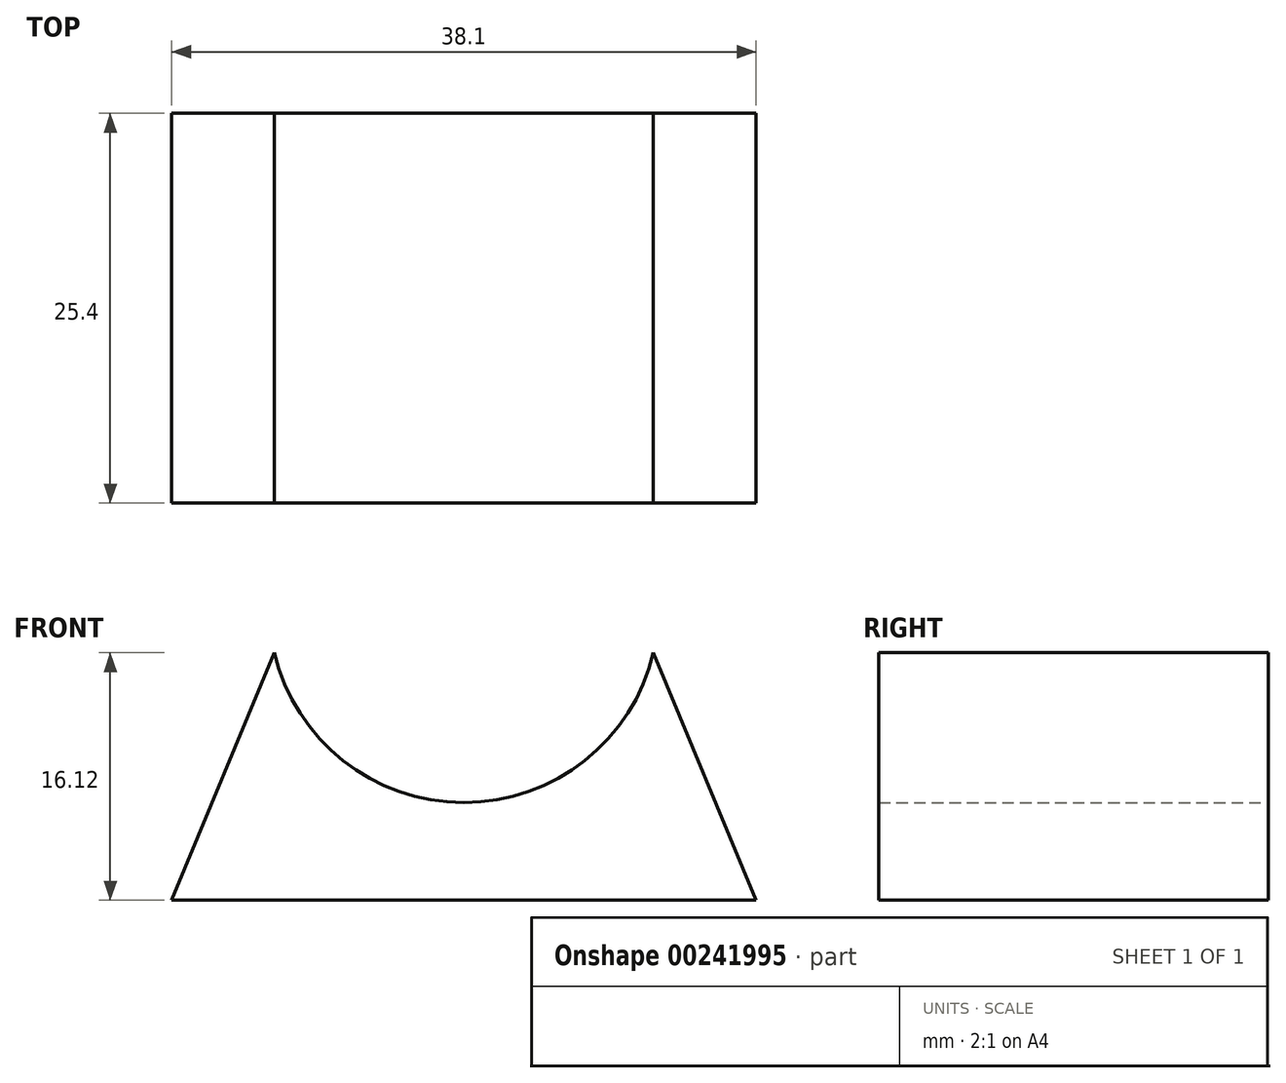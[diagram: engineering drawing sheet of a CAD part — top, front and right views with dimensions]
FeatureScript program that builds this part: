
annotation { "Feature Type Name" : "Feature", "Feature Type Description" : "" }
export const myFeature = defineFeature(function(context is Context, id is Id, definition is map)
    precondition{}
    {
        {
            var Q0;
            Q0=qCreatedBy(makeId("Front.planeOp"),FACE);
            var sketch = newSketch(context, id + "F0", { "sketchPlane" : qUnion([Q0])});
            skLineSegment(sketch, "E0", {"start": v(0, 0) * mm, "end": v(38.1, 0) * mm});
            skLineSegment(sketch, "E1", {"start": v(19.05, 0) * mm, "end": v(19.05, 6.35) * mm});
            skArc(sketch, "E2", {"start": v(6.7, 16.12) * mm, "mid": v(19.05, 6.35) * mm, "end": v(31.4, 16.12) * mm});
            skLineSegment(sketch, "E3", {"start": v(0, 0) * mm, "end": v(6.7, 16.12) * mm});
            skLineSegment(sketch, "E4", {"start": v(31.4, 16.12) * mm, "end": v(38.1, 0) * mm});
            skLineSegment(sketch, "E5.trimOffspring", {"start": v(19.05, 16.12) * mm, "end": v(19.05, 19.05) * mm});
            skSolve(sketch);
        }
        {
            var Q0;
            Q0 = qSketchRegion(id + "F0", true);
            extrude(context, id + "F1", {"entities" : qUnion([Q0]), "depth" : 25.4 * mm});
        }
    });
